# Revit family: ALE A25_60_C50
name_source: partatom
category: Equipement spécialisé
revit_build: Autodesk Revit 2017 (Build: 20160225_1515(x64)
units: mm (PartAtom-declared; Revit-internal decimal feet)

## family parameters
Basée sur le plan de construction = Non
Cote de connecteur circulaire = Utiliser le diamètre
Couper avec des vides une fois chargée = Non
Partagée = Non
Point de calcul de pièce = Non
Toujours verticalement = Oui
Type d'élément = Normal

## types (1)
- Borne Escamotable A25_60_C50
    Fabricant = AMCO Les Escamotables
    Largeur_plaque = 330 mm
    Longueur_plaque = 450 mm  [stored 1.47638 ft]
    Matériau_Massif = MASSIF BETON
    Matériau_borne = POSTE ESCAMOTABLE GRIS
    Matériau_plaque = PLAQUE AU SOL
    Modèle = ALE 25-60-C50
    URL = http://bornes-escamotables.com
    diamètre_borne = 250 mm  [stored 0.82021 ft]
    e_cap = 20 mm  [stored 0.0656168 ft]
    epaisseur_plaque = 20 mm  [stored 0.0656168 ft]
    hauteur_borne = 600 mm
    hauteur_massif = 990 mm  [stored 3.24803 ft]
    l1_plaque = 170 mm  [stored 0.557743 ft]
    l2_plaque = 280 mm
    largeur_massif = 600 mm
    longueur_massif = 730 mm  [stored 2.39501 ft]
    rayon_vide = 125 mm  [stored 0.410105 ft]

note: [stored X ft] marks values corroborated as IEEE doubles in the binary element streams (Revit-internal decimal feet)
